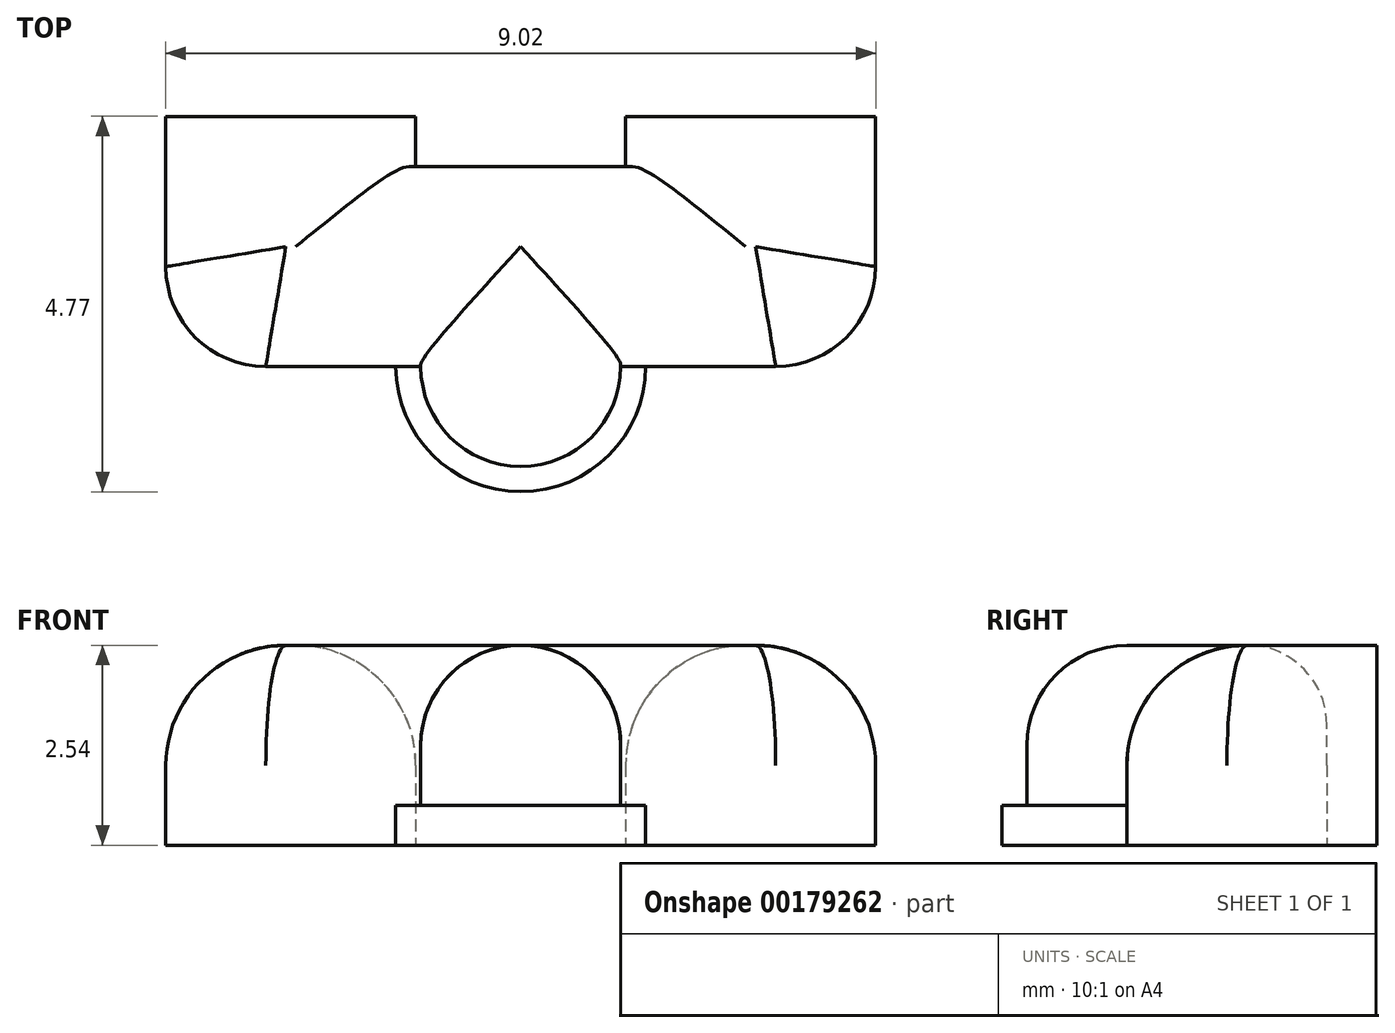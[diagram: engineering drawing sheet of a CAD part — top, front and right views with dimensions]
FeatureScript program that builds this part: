
annotation { "Feature Type Name" : "Feature", "Feature Type Description" : "" }
export const myFeature = defineFeature(function(context is Context, id is Id, definition is map)
    precondition{}
    {
        {
            var Q0;
            Q0=qCreatedBy(makeId("Top.planeOp"),FACE);
            var sketch = newSketch(context, id + "F0", { "sketchPlane" : qUnion([Q0])});
            skLineSegment(sketch, "E0", {"start": v(0, 0) * mm, "end": v(4.5, 0) * mm});
            skLineSegment(sketch, "E1", {"start": v(4.5, 0) * mm, "end": v(4.5, 3.17) * mm});
            skLineSegment(sketch, "E2", {"start": v(4.5, 3.18) * mm, "end": v(1.33, 3.17) * mm});
            skLineSegment(sketch, "E3", {"start": v(1.33, 3.18) * mm, "end": v(1.33, 2.54) * mm});
            skLineSegment(sketch, "E4", {"start": v(1.33, 2.54) * mm, "end": v(0, 2.54) * mm});
            skLineSegment(sketch, "E5", {"start": v(0, 2.54) * mm, "end": v(0, 0) * mm});
            skLineSegment(sketch, "E6.MirrorCS", {"start": v(-1.33, 2.54) * mm, "end": v(0, 2.54) * mm});
            skLineSegment(sketch, "E7.MirrorCS", {"start": v(-1.33, 3.18) * mm, "end": v(-1.33, 2.54) * mm});
            skLineSegment(sketch, "E8.MirrorCS", {"start": v(-4.5, 3.17) * mm, "end": v(-1.33, 3.18) * mm});
            skLineSegment(sketch, "E9.MirrorCS", {"start": v(-4.5, 0) * mm, "end": v(-4.5, 3.17) * mm});
            skLineSegment(sketch, "E10.MirrorCS", {"start": v(0, 0) * mm, "end": v(-4.5, 0) * mm});
            skLineSegment(sketch, "E11", {"start": v(0, 0) * mm, "end": v(0, -1.27) * mm});
            skLineSegment(sketch, "E12", {"start": v(0, -1.27) * mm, "end": v(1.27, -1.27) * mm});
            skLineSegment(sketch, "E13", {"start": v(1.27, -1.27) * mm, "end": v(1.27, 0) * mm});
            skLineSegment(sketch, "E14.MirrorCS", {"start": v(-1.27, -1.27) * mm, "end": v(-1.27, 0) * mm});
            skLineSegment(sketch, "E15.MirrorCS", {"start": v(0, -1.27) * mm, "end": v(-1.27, -1.27) * mm});
            skSolve(sketch);
        }
        {
            var Q0;
            Q0 = qSketchRegion(id + "F0", true);
            extrude(context, id + "F1", {"entities" : qUnion([Q0]), "depth" : 2.54 * mm});
        }
        {
            var Q0;
            Q0=makeQuery(id+"F1.opExtrude","SWEPT_EDGE",EDGE,{"disambiguationData":[OSD([sQuery(id+"F0.wireOp",EDGE,"E9.MirrorCS"),sQuery(id+"F0.wireOp",EDGE,"E10.MirrorCS")])]});
            var Q1;
            Q1=makeQuery(id+"F1.opExtrude","SWEPT_EDGE",EDGE,{"disambiguationData":[OSD([sQuery(id+"F0.wireOp",EDGE,"E0"),sQuery(id+"F0.wireOp",EDGE,"E1")])]});
            fillet(context, id + "F2", {"entities" : qUnion([Q0, Q1]), "radius" : 1.27 * mm, "tangentPropagation" : true, "allowEdgeOverflow" : false});
        }
        {
            var Q0;
            Q0=makeQuery(id+"F1.opExtrude","CAP_EDGE",EDGE,{"disambiguationData":[OSD([sQuery(id+"F0.wireOp",EDGE,"E12"),sQuery(id+"F0.wireOp",EDGE,"E15.MirrorCS")])],"isStart":false});
            fillet(context, id + "F3", {"entities" : qUnion([Q0]), "radius" : 1.27 * mm, "tangentPropagation" : true, "allowEdgeOverflow" : false});
        }
        {
            var Q0;
            Q0=makeQuery(id+"F1.opExtrude","CAP_EDGE",EDGE,{"disambiguationData":[OSD([sQuery(id+"F0.wireOp",EDGE,"E9.MirrorCS")])],"isStart":false});
            var Q1;
            Q1=makeQuery(id+"F1.opExtrude","CAP_EDGE",EDGE,{"disambiguationData":[OSD([sQuery(id+"F0.wireOp",EDGE,"E1")])],"isStart":false});
            var Q2;
            Q2=makeQuery(id+"F1.opExtrude","CAP_EDGE",EDGE,{"disambiguationData":[OSD([sQuery(id+"F0.wireOp",EDGE,"E3")])],"isStart":false});
            var Q3;
            Q3=makeQuery(id+"F1.opExtrude","CAP_EDGE",EDGE,{"disambiguationData":[OSD([sQuery(id+"F0.wireOp",EDGE,"E7.MirrorCS")])],"isStart":false});
            fillet(context, id + "F4", {"entities" : qUnion([Q0, Q1, Q2, Q3]), "radius" : 1.52 * mm, "tangentPropagation" : true, "allowEdgeOverflow" : false});
        }
        {
            var Q0;
            Q0=makeQuery(id+"F1.opExtrude","SWEPT_EDGE",EDGE,{"disambiguationData":[OSD([sQuery(id+"F0.wireOp",EDGE,"E12"),sQuery(id+"F0.wireOp",EDGE,"E13")])]});
            var Q1;
            Q1=makeQuery(id+"F1.opExtrude","SWEPT_EDGE",EDGE,{"disambiguationData":[OSD([sQuery(id+"F0.wireOp",EDGE,"E14.MirrorCS"),sQuery(id+"F0.wireOp",EDGE,"E15.MirrorCS")])]});
            fillet(context, id + "F5", {"entities" : qUnion([Q0, Q1]), "radius" : 1.27 * mm, "tangentPropagation" : true, "allowEdgeOverflow" : false});
        }
        {
            var Q0;
            Q0=makeQuery(id+"F1.opExtrude","CAP_EDGE",EDGE,{"disambiguationData":[OSD([sQuery(id+"F0.wireOp",EDGE,"E4"),sQuery(id+"F0.wireOp",EDGE,"E6.MirrorCS")])],"isStart":false});
            fillet(context, id + "F6", {"entities" : qUnion([Q0]), "radius" : 1.02 * mm, "tangentPropagation" : true, "allowEdgeOverflow" : false});
        }
        {
            var Q0;
            Q0=qCreatedBy(makeId("Top.planeOp"),FACE);
            var sketch = newSketch(context, id + "F7", { "sketchPlane" : qUnion([Q0])});
            skCircle(sketch, "E16", {"center": v(0, 0) * mm, "radius": 1.59 * mm});
            skLineSegment(sketch, "E17", {"start": v(0, 0) * mm, "end": v(-1.59, 0) * mm});
            skLineSegment(sketch, "E18", {"start": v(-1.59, 0) * mm, "end": v(0, 0) * mm});
            skSolve(sketch);
        }
        {
            var Q0;
            Q0 = qSketchRegion(id + "F7", true);
            extrude(context, id + "F8", {"entities" : qUnion([Q0]), "operationType" : NewBodyOperationType.ADD, "depth" : 0.5 * mm});
        }
    });
